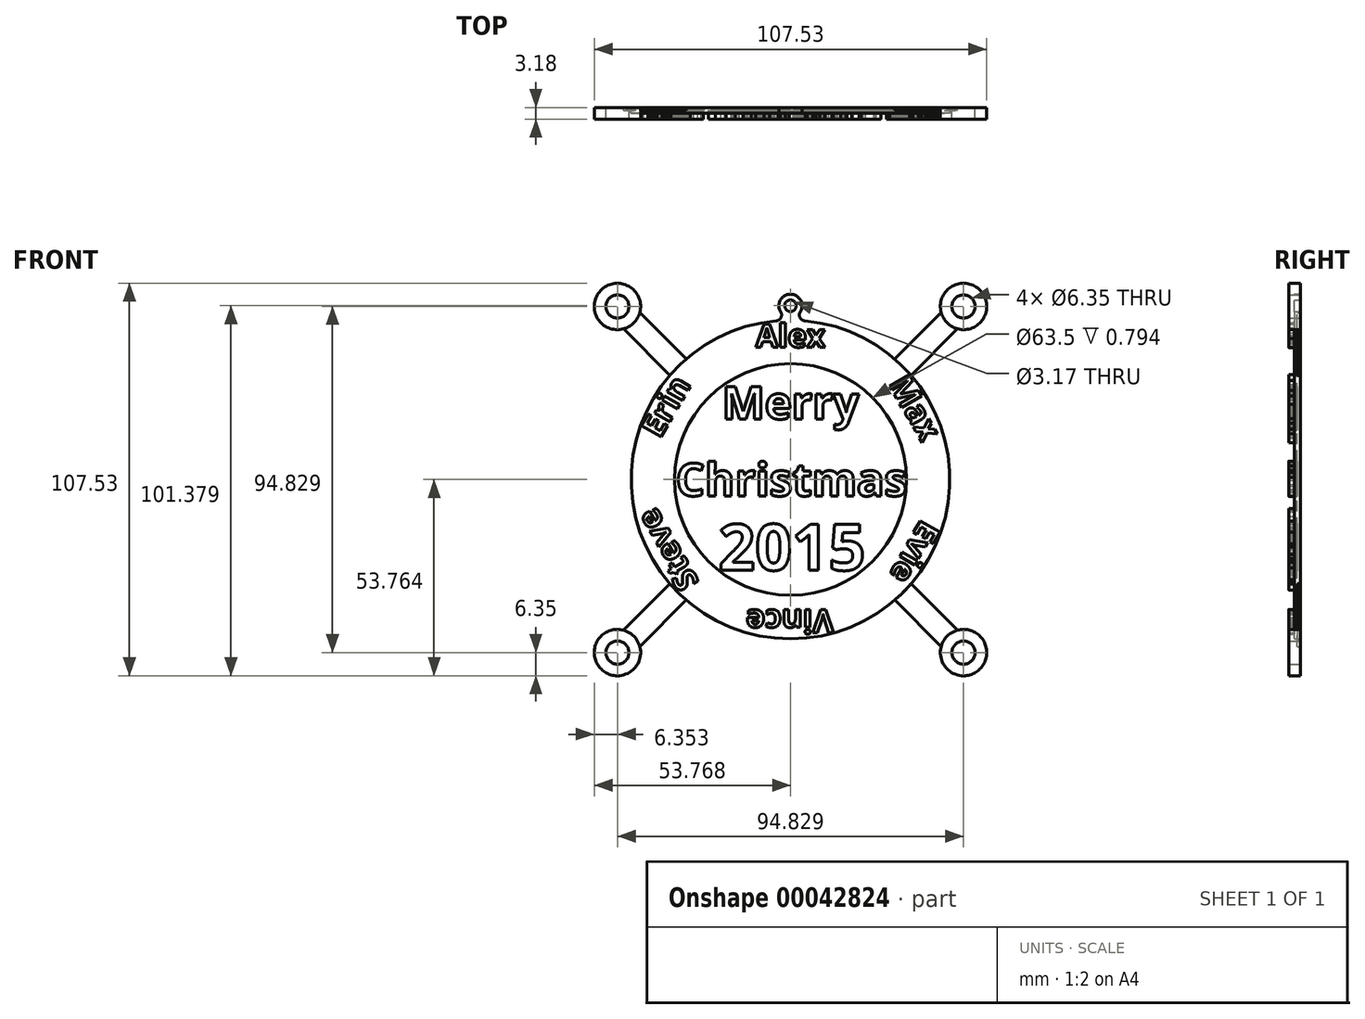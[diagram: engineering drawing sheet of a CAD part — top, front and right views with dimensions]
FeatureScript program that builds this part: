
annotation { "Feature Type Name" : "Feature", "Feature Type Description" : "" }
export const myFeature = defineFeature(function(context is Context, id is Id, definition is map)
    precondition{}
    {
        {
            var Q0;
            Q0=qCreatedBy(makeId("Front.planeOp"),FACE);
            var sketch = newSketch(context, id + "F0", { "sketchPlane" : qUnion([Q0])});
            skText(sketch, "E0", { "text": "2015", "fontName": "OpenSans-Bold.ttf"});
            skPoint(sketch, "E1.center", {"position": v(-132.38, 12.9) * mm});
            skCircle(sketch, "E1.3.1", {"center": v(-84.97, -34.52) * mm, "radius": 6.35 * mm});
            skText(sketch, "E2", { "text": "Christmas", "fontName": "OpenSans-Bold.ttf"});
            skArc(sketch, "E3", {"start": v(-136.26, 56.38) * mm, "mid": v(-132.38, -30.76) * mm, "end": v(-128.5, 56.38) * mm});
            skCircle(sketch, "E4", {"center": v(-132.38, 12.9) * mm, "radius": 31.75 * mm});
            skLineSegment(sketch, "E5", {"start": v(-132.38, 12.9) * mm, "end": v(-132.38, 89.83) * mm, "construction": true});
            skLineSegment(sketch, "E1.2.3", {"start": v(-160.93, -20.14) * mm, "end": v(-173.66, -32.88) * mm});
            skLineSegment(sketch, "E1.2.0", {"start": v(-178.15, -28.39) * mm, "end": v(-165.42, -15.65) * mm});
            skLineSegment(sketch, "E6", {"start": v(-86.61, 54.18) * mm, "end": v(-99.35, 41.44) * mm});
            skPoint(sketch, "E7.orphan", {"position": v(-132.38, 42.36) * mm});
            skCircle(sketch, "E1.1.1", {"center": v(-179.8, 60.3) * mm, "radius": 6.35 * mm});
            skLineSegment(sketch, "E8", {"start": v(-103.84, 45.93) * mm, "end": v(-91.1, 58.67) * mm});
            skLineSegment(sketch, "E1.3.3", {"start": v(-99.35, -15.65) * mm, "end": v(-86.61, -28.39) * mm});
            skLineSegment(sketch, "E9", {"start": v(-132.38, 12.9) * mm, "end": v(-73.52, 71.76) * mm, "construction": true});
            skLineSegment(sketch, "E1.3.0", {"start": v(-91.1, -32.88) * mm, "end": v(-103.84, -20.14) * mm});
            skCircle(sketch, "E10", {"center": v(-84.97, 60.3) * mm, "radius": 6.35 * mm});
            skLineSegment(sketch, "E1.1.0", {"start": v(-173.66, 58.67) * mm, "end": v(-160.93, 45.93) * mm});
            skLineSegment(sketch, "E1.1.3", {"start": v(-165.42, 41.44) * mm, "end": v(-178.15, 54.18) * mm});
            skCircle(sketch, "E1.2.1", {"center": v(-179.8, -34.52) * mm, "radius": 6.35 * mm});
            skText(sketch, "E11", { "text": "Evie", "fontName": "OpenSans-Bold.ttf"});
            skText(sketch, "E12", { "text": "Merry", "fontName": "OpenSans-Bold.ttf"});
            skLineSegment(sketch, "E13.4.0", {"start": v(-104.89, -2.98) * mm, "end": v(-101.38, -5) * mm, "construction": true});
            skText(sketch, "E14", { "text": "Vince", "fontName": "OpenSans-Bold.ttf"});
            skText(sketch, "E15", { "text": "Erin", "fontName": "OpenSans-Bold.ttf"});
            skText(sketch, "E16", { "text": "Max", "fontName": "OpenSans-Bold.ttf"});
            skLineSegment(sketch, "E13.5.0", {"start": v(-104.89, 28.77) * mm, "end": v(-101.38, 30.8) * mm, "construction": true});
            skCircle(sketch, "E1.3.2", {"center": v(-84.97, -34.52) * mm, "radius": 3.18 * mm});
            skCircle(sketch, "E1.2.2", {"center": v(-179.8, -34.52) * mm, "radius": 3.18 * mm});
            skText(sketch, "E17", { "text": "Steve", "fontName": "OpenSans-Bold.ttf"});
            skLineSegment(sketch, "E13.3.0", {"start": v(-132.38, -18.86) * mm, "end": v(-132.38, -22.9) * mm, "construction": true});
            skCircle(sketch, "E1.1.2", {"center": v(-179.8, 60.3) * mm, "radius": 3.18 * mm});
            skLineSegment(sketch, "E13.2.0", {"start": v(-159.88, -2.98) * mm, "end": v(-163.39, -5) * mm, "construction": true});
            skText(sketch, "E18", { "text": "Alex", "fontName": "OpenSans-Bold.ttf"});
            skLineSegment(sketch, "E13.1.0", {"start": v(-159.88, 28.77) * mm, "end": v(-163.39, 30.8) * mm, "construction": true});
            skCircle(sketch, "E19", {"center": v(-84.97, 60.3) * mm, "radius": 3.18 * mm});
            skLineSegment(sketch, "E20.1.0", {"start": v(-160.12, 28.9) * mm, "end": v(-165.6, 32.08) * mm, "construction": true});
            skLineSegment(sketch, "E21.MirrorCS", {"start": v(-101.44, -6.5) * mm, "end": v(-95.1, -6.5) * mm, "construction": true});
            skArc(sketch, "E22", {"start": v(-129.7, 58.8) * mm, "mid": v(-132.38, 63.68) * mm, "end": v(-135.06, 58.8) * mm});
            skLineSegment(sketch, "E23", {"start": v(-132.38, 44.64) * mm, "end": v(-132.38, 48.7) * mm, "construction": true});
            skCircle(sketch, "E24", {"center": v(-132.38, 60.5) * mm, "radius": 1.59 * mm});
            skArc(sketch, "E25.filletArc", {"start": v(-136.26, 56.38) * mm, "mid": v(-134.98, 57.26) * mm, "end": v(-135.06, 58.8) * mm});
            skArc(sketch, "E26.filletArc", {"start": v(-129.7, 58.8) * mm, "mid": v(-129.78, 57.26) * mm, "end": v(-128.5, 56.38) * mm});
            const initialGuessF0  = {"E0": [-0.15212, -0.01197, 1, 0, 0.0127], "E2": [-0.16381, 0.0084, 1, 0, 0.009], "E11": [-0.09647, 0.00225, -0.5, -0.86603, 0.00635], "E12": [-0.1512, 0.02947, 1, 0, 0.009], "E14": [-0.12059, -0.0228, -1, 0, 0.00635], "E15": [-0.16818, 0.02388, 0.5, 0.86603, 0.00635], "E16": [-0.10562, 0.03914, 0.5, -0.86603, 0.00635], "E17": [-0.15733, -0.01522, -0.5, 0.86603, 0.00635], "E18": [-0.1419, 0.04915, 1, 0, 0.00635]};
            skSetInitialGuess(sketch, initialGuessF0);
            skSolve(sketch);
        }
        {
            var Q0;
            Q0=makeQuery(id+"F0.imprint","IMPRINT",FACE,{"disambiguationData":[TD([[makeQuery(id+"F0.imprint","IMPRINT",EDGE,{"derivedFrom":sQuery(id+"F0.wireOp",EDGE,"E18.sketch_text.stroke-0")}),-1.0]])]});
            var Q1;
            Q1=makeQuery(id+"F0.imprint","IMPRINT",FACE,{"disambiguationData":[TD([[makeQuery(id+"F0.imprint","IMPRINT",EDGE,{"derivedFrom":sQuery(id+"F0.wireOp",EDGE,"E18.sketch_text.stroke-12")}),-1.0]])]});
            var Q2;
            Q2=makeQuery(id+"F0.imprint","IMPRINT",FACE,{"disambiguationData":[TD([[makeQuery(id+"F0.imprint","IMPRINT",EDGE,{"derivedFrom":sQuery(id+"F0.wireOp",EDGE,"E18.sketch_text.stroke-16")}),-1.0]])]});
            var Q3;
            Q3=makeQuery(id+"F0.imprint","IMPRINT",FACE,{"disambiguationData":[TD([[makeQuery(id+"F0.imprint","IMPRINT",EDGE,{"derivedFrom":sQuery(id+"F0.wireOp",EDGE,"E18.sketch_text.stroke-36")}),-1.0]])]});
            var Q4;
            Q4=makeQuery(id+"F0.imprint","IMPRINT",FACE,{"disambiguationData":[TD([[makeQuery(id+"F0.imprint","IMPRINT",EDGE,{"derivedFrom":sQuery(id+"F0.wireOp",EDGE,"E16.sketch_text.stroke-0")}),-1.0]])]});
            var Q5;
            Q5=makeQuery(id+"F0.imprint","IMPRINT",FACE,{"disambiguationData":[TD([[makeQuery(id+"F0.imprint","IMPRINT",EDGE,{"derivedFrom":sQuery(id+"F0.wireOp",EDGE,"E16.sketch_text.stroke-19")}),-1.0]])]});
            var Q6;
            Q6=makeQuery(id+"F0.imprint","IMPRINT",FACE,{"disambiguationData":[TD([[makeQuery(id+"F0.imprint","IMPRINT",EDGE,{"derivedFrom":sQuery(id+"F0.wireOp",EDGE,"E16.sketch_text.stroke-44")}),-1.0]])]});
            var Q7;
            Q7=makeQuery(id+"F0.imprint","IMPRINT",FACE,{"disambiguationData":[TD([[makeQuery(id+"F0.imprint","IMPRINT",EDGE,{"derivedFrom":sQuery(id+"F0.wireOp",EDGE,"E12.sketch_text.stroke-0")}),-1.0]])]});
            var Q8;
            Q8=makeQuery(id+"F0.imprint","IMPRINT",FACE,{"disambiguationData":[TD([[makeQuery(id+"F0.imprint","IMPRINT",EDGE,{"derivedFrom":sQuery(id+"F0.wireOp",EDGE,"E12.sketch_text.stroke-19")}),-1.0]])]});
            var Q9;
            Q9=makeQuery(id+"F0.imprint","IMPRINT",FACE,{"disambiguationData":[TD([[makeQuery(id+"F0.imprint","IMPRINT",EDGE,{"derivedFrom":sQuery(id+"F0.wireOp",EDGE,"E12.sketch_text.stroke-39")}),-1.0]])]});
            var Q10;
            Q10=makeQuery(id+"F0.imprint","IMPRINT",FACE,{"disambiguationData":[TD([[makeQuery(id+"F0.imprint","IMPRINT",EDGE,{"derivedFrom":sQuery(id+"F0.wireOp",EDGE,"E12.sketch_text.stroke-52")}),-1.0]])]});
            var Q11;
            Q11=makeQuery(id+"F0.imprint","IMPRINT",FACE,{"disambiguationData":[TD([[makeQuery(id+"F0.imprint","IMPRINT",EDGE,{"derivedFrom":sQuery(id+"F0.wireOp",EDGE,"E12.sketch_text.stroke-65")}),-1.0]])]});
            var Q12;
            Q12=makeQuery(id+"F0.imprint","IMPRINT",FACE,{"disambiguationData":[TD([[makeQuery(id+"F0.imprint","IMPRINT",EDGE,{"derivedFrom":sQuery(id+"F0.wireOp",EDGE,"E2.sketch_text.stroke-0")}),-1.0]])]});
            var Q13;
            Q13=makeQuery(id+"F0.imprint","IMPRINT",FACE,{"disambiguationData":[TD([[makeQuery(id+"F0.imprint","IMPRINT",EDGE,{"derivedFrom":sQuery(id+"F0.wireOp",EDGE,"E2.sketch_text.stroke-15")}),-1.0]])]});
            var Q14;
            Q14=makeQuery(id+"F0.imprint","IMPRINT",FACE,{"disambiguationData":[TD([[makeQuery(id+"F0.imprint","IMPRINT",EDGE,{"derivedFrom":sQuery(id+"F0.wireOp",EDGE,"E2.sketch_text.stroke-32")}),-1.0]])]});
            var Q15;
            Q15=makeQuery(id+"F0.imprint","IMPRINT",FACE,{"disambiguationData":[TD([[makeQuery(id+"F0.imprint","IMPRINT",EDGE,{"derivedFrom":sQuery(id+"F0.wireOp",EDGE,"E2.sketch_text.stroke-50")}),-1.0]])]});
            var Q16;
            Q16=makeQuery(id+"F0.imprint","IMPRINT",FACE,{"disambiguationData":[TD([[makeQuery(id+"F0.imprint","IMPRINT",EDGE,{"derivedFrom":sQuery(id+"F0.wireOp",EDGE,"E2.sketch_text.stroke-54")}),-1.0]])]});
            var Q17;
            Q17=makeQuery(id+"F0.imprint","IMPRINT",FACE,{"disambiguationData":[TD([[makeQuery(id+"F0.imprint","IMPRINT",EDGE,{"derivedFrom":sQuery(id+"F0.wireOp",EDGE,"E2.sketch_text.stroke-45")}),-1.0]])]});
            var Q18;
            Q18=makeQuery(id+"F0.imprint","IMPRINT",FACE,{"disambiguationData":[TD([[makeQuery(id+"F0.imprint","IMPRINT",EDGE,{"derivedFrom":sQuery(id+"F0.wireOp",EDGE,"E2.sketch_text.stroke-80")}),-1.0]])]});
            var Q19;
            Q19=makeQuery(id+"F0.imprint","IMPRINT",FACE,{"disambiguationData":[TD([[makeQuery(id+"F0.imprint","IMPRINT",EDGE,{"derivedFrom":sQuery(id+"F0.wireOp",EDGE,"E2.sketch_text.stroke-98")}),-1.0]])]});
            var Q20;
            Q20=makeQuery(id+"F0.imprint","IMPRINT",FACE,{"disambiguationData":[TD([[makeQuery(id+"F0.imprint","IMPRINT",EDGE,{"derivedFrom":sQuery(id+"F0.wireOp",EDGE,"E2.sketch_text.stroke-126")}),-1.0]])]});
            var Q21;
            Q21=makeQuery(id+"F0.imprint","IMPRINT",FACE,{"disambiguationData":[TD([[makeQuery(id+"F0.imprint","IMPRINT",EDGE,{"derivedFrom":sQuery(id+"F0.wireOp",EDGE,"E2.sketch_text.stroke-151")}),-1.0]])]});
            var Q22;
            Q22=makeQuery(id+"F0.imprint","IMPRINT",FACE,{"disambiguationData":[TD([[makeQuery(id+"F0.imprint","IMPRINT",EDGE,{"derivedFrom":sQuery(id+"F0.wireOp",EDGE,"E0.sketch_text.stroke-0")}),-1.0]])]});
            var Q23;
            Q23=makeQuery(id+"F0.imprint","IMPRINT",FACE,{"disambiguationData":[TD([[makeQuery(id+"F0.imprint","IMPRINT",EDGE,{"derivedFrom":sQuery(id+"F0.wireOp",EDGE,"E0.sketch_text.stroke-24")}),-1.0]])]});
            var Q24;
            Q24=makeQuery(id+"F0.imprint","IMPRINT",FACE,{"disambiguationData":[TD([[makeQuery(id+"F0.imprint","IMPRINT",EDGE,{"derivedFrom":sQuery(id+"F0.wireOp",EDGE,"E0.sketch_text.stroke-40")}),-1.0]])]});
            var Q25;
            Q25=makeQuery(id+"F0.imprint","IMPRINT",FACE,{"disambiguationData":[TD([[makeQuery(id+"F0.imprint","IMPRINT",EDGE,{"derivedFrom":sQuery(id+"F0.wireOp",EDGE,"E0.sketch_text.stroke-50")}),-1.0]])]});
            var Q26;
            Q26=makeQuery(id+"F0.imprint","IMPRINT",FACE,{"disambiguationData":[TD([[makeQuery(id+"F0.imprint","IMPRINT",EDGE,{"derivedFrom":sQuery(id+"F0.wireOp",EDGE,"E11.sketch_text.stroke-0")}),-1.0]])]});
            var Q27;
            Q27=makeQuery(id+"F0.imprint","IMPRINT",FACE,{"disambiguationData":[TD([[makeQuery(id+"F0.imprint","IMPRINT",EDGE,{"derivedFrom":sQuery(id+"F0.wireOp",EDGE,"E11.sketch_text.stroke-12")}),-1.0]])]});
            var Q28;
            Q28=makeQuery(id+"F0.imprint","IMPRINT",FACE,{"disambiguationData":[TD([[makeQuery(id+"F0.imprint","IMPRINT",EDGE,{"derivedFrom":sQuery(id+"F0.wireOp",EDGE,"E11.sketch_text.stroke-27")}),-1.0]])]});
            var Q29;
            Q29=makeQuery(id+"F0.imprint","IMPRINT",FACE,{"disambiguationData":[TD([[makeQuery(id+"F0.imprint","IMPRINT",EDGE,{"derivedFrom":sQuery(id+"F0.wireOp",EDGE,"E11.sketch_text.stroke-22")}),-1.0]])]});
            var Q30;
            Q30=makeQuery(id+"F0.imprint","IMPRINT",FACE,{"disambiguationData":[TD([[makeQuery(id+"F0.imprint","IMPRINT",EDGE,{"derivedFrom":sQuery(id+"F0.wireOp",EDGE,"E11.sketch_text.stroke-31")}),-1.0]])]});
            var Q31;
            Q31=makeQuery(id+"F0.imprint","IMPRINT",FACE,{"disambiguationData":[TD([[makeQuery(id+"F0.imprint","IMPRINT",EDGE,{"derivedFrom":sQuery(id+"F0.wireOp",EDGE,"E14.sketch_text.stroke-0")}),-1.0]])]});
            var Q32;
            Q32=makeQuery(id+"F0.imprint","IMPRINT",FACE,{"disambiguationData":[TD([[makeQuery(id+"F0.imprint","IMPRINT",EDGE,{"derivedFrom":sQuery(id+"F0.wireOp",EDGE,"E14.sketch_text.stroke-15")}),-1.0]])]});
            var Q33;
            Q33=makeQuery(id+"F0.imprint","IMPRINT",FACE,{"disambiguationData":[TD([[makeQuery(id+"F0.imprint","IMPRINT",EDGE,{"derivedFrom":sQuery(id+"F0.wireOp",EDGE,"E14.sketch_text.stroke-10")}),-1.0]])]});
            var Q34;
            Q34=makeQuery(id+"F0.imprint","IMPRINT",FACE,{"disambiguationData":[TD([[makeQuery(id+"F0.imprint","IMPRINT",EDGE,{"derivedFrom":sQuery(id+"F0.wireOp",EDGE,"E14.sketch_text.stroke-19")}),-1.0]])]});
            var Q35;
            Q35=makeQuery(id+"F0.imprint","IMPRINT",FACE,{"disambiguationData":[TD([[makeQuery(id+"F0.imprint","IMPRINT",EDGE,{"derivedFrom":sQuery(id+"F0.wireOp",EDGE,"E14.sketch_text.stroke-36")}),-1.0]])]});
            var Q36;
            Q36=makeQuery(id+"F0.imprint","IMPRINT",FACE,{"disambiguationData":[TD([[makeQuery(id+"F0.imprint","IMPRINT",EDGE,{"derivedFrom":sQuery(id+"F0.wireOp",EDGE,"E14.sketch_text.stroke-50")}),-1.0]])]});
            var Q37;
            Q37=makeQuery(id+"F0.imprint","IMPRINT",FACE,{"disambiguationData":[TD([[makeQuery(id+"F0.imprint","IMPRINT",EDGE,{"derivedFrom":sQuery(id+"F0.wireOp",EDGE,"E17.sketch_text.stroke-0")}),-1.0]])]});
            var Q38;
            Q38=makeQuery(id+"F0.imprint","IMPRINT",FACE,{"disambiguationData":[TD([[makeQuery(id+"F0.imprint","IMPRINT",EDGE,{"derivedFrom":sQuery(id+"F0.wireOp",EDGE,"E17.sketch_text.stroke-28")}),-1.0]])]});
            var Q39;
            Q39=makeQuery(id+"F0.imprint","IMPRINT",FACE,{"disambiguationData":[TD([[makeQuery(id+"F0.imprint","IMPRINT",EDGE,{"derivedFrom":sQuery(id+"F0.wireOp",EDGE,"E17.sketch_text.stroke-46")}),-1.0]])]});
            var Q40;
            Q40=makeQuery(id+"F0.imprint","IMPRINT",FACE,{"disambiguationData":[TD([[makeQuery(id+"F0.imprint","IMPRINT",EDGE,{"derivedFrom":sQuery(id+"F0.wireOp",EDGE,"E17.sketch_text.stroke-66")}),-1.0]])]});
            var Q41;
            Q41=makeQuery(id+"F0.imprint","IMPRINT",FACE,{"disambiguationData":[TD([[makeQuery(id+"F0.imprint","IMPRINT",EDGE,{"derivedFrom":sQuery(id+"F0.wireOp",EDGE,"E17.sketch_text.stroke-76")}),-1.0]])]});
            var Q42;
            Q42=makeQuery(id+"F0.imprint","IMPRINT",FACE,{"disambiguationData":[TD([[makeQuery(id+"F0.imprint","IMPRINT",EDGE,{"derivedFrom":sQuery(id+"F0.wireOp",EDGE,"E15.sketch_text.stroke-0")}),-1.0]])]});
            var Q43;
            Q43=makeQuery(id+"F0.imprint","IMPRINT",FACE,{"disambiguationData":[TD([[makeQuery(id+"F0.imprint","IMPRINT",EDGE,{"derivedFrom":sQuery(id+"F0.wireOp",EDGE,"E15.sketch_text.stroke-12")}),-1.0]])]});
            var Q44;
            Q44=makeQuery(id+"F0.imprint","IMPRINT",FACE,{"disambiguationData":[TD([[makeQuery(id+"F0.imprint","IMPRINT",EDGE,{"derivedFrom":sQuery(id+"F0.wireOp",EDGE,"E15.sketch_text.stroke-30")}),-1.0]])]});
            var Q45;
            Q45=makeQuery(id+"F0.imprint","IMPRINT",FACE,{"disambiguationData":[TD([[makeQuery(id+"F0.imprint","IMPRINT",EDGE,{"derivedFrom":sQuery(id+"F0.wireOp",EDGE,"E15.sketch_text.stroke-25")}),-1.0]])]});
            var Q46;
            Q46=makeQuery(id+"F0.imprint","IMPRINT",FACE,{"disambiguationData":[TD([[makeQuery(id+"F0.imprint","IMPRINT",EDGE,{"derivedFrom":sQuery(id+"F0.wireOp",EDGE,"E15.sketch_text.stroke-34")}),-1.0]])]});
            var Q47;
            Q47=makeQuery(id+"F0.imprint","IMPRINT",FACE,{"disambiguationData":[TD([[makeQuery(id+"F0.imprint","IMPRINT",EDGE,{"derivedFrom":sQuery(id+"F0.wireOp",EDGE,"E1.1.2")}),-1.0]])]});
            var Q48;
            Q48=makeQuery(id+"F0.imprint","IMPRINT",FACE,{"disambiguationData":[TD([[makeQuery(id+"F0.imprint","IMPRINT",EDGE,{"derivedFrom":sQuery(id+"F0.wireOp",EDGE,"E19")}),-1.0]])]});
            var Q49;
            Q49=makeQuery(id+"F0.imprint","IMPRINT",FACE,{"disambiguationData":[TD([[makeQuery(id+"F0.imprint","IMPRINT",EDGE,{"derivedFrom":sQuery(id+"F0.wireOp",EDGE,"E1.3.2")}),-1.0]])]});
            var Q50;
            Q50=makeQuery(id+"F0.imprint","IMPRINT",FACE,{"disambiguationData":[TD([[makeQuery(id+"F0.imprint","IMPRINT",EDGE,{"derivedFrom":sQuery(id+"F0.wireOp",EDGE,"E1.2.2")}),-1.0]])]});
            extrude(context, id + "F1", {"entities" : qUnion([Q0, Q1, Q2, Q3, Q4, Q5, Q6, Q7, Q8, Q9, Q10, Q11, Q12, Q13, Q14, Q15, Q16, Q17, Q18, Q19, Q20, Q21, Q22, Q23, Q24, Q25, Q26, Q27, Q28, Q29, Q30, Q31, Q32, Q33, Q34, Q35, Q36, Q37, Q38, Q39, Q40, Q41, Q42, Q43, Q44, Q45, Q46, Q47, Q48, Q49, Q50]), "depth" : 3.17 * mm});
        }
        {
            var Q0;
            Q0=makeQuery(id+"F0.imprint","IMPRINT",FACE,{"disambiguationData":[TD([[makeQuery(id+"F0.imprint","IMPRINT",EDGE,{"derivedFrom":sQuery(id+"F0.wireOp",EDGE,"E4")}),-1.0]])]});
            var Q1;
            Q1=makeQuery(id+"F0.imprint","IMPRINT",FACE,{"disambiguationData":[TD([[makeQuery(id+"F0.imprint","IMPRINT",EDGE,{"derivedFrom":sQuery(id+"F0.wireOp",EDGE,"E17.sketch_text.stroke-46")}),1.0]])]});
            var Q2;
            Q2=makeQuery(id+"F0.imprint","IMPRINT",FACE,{"disambiguationData":[TD([[makeQuery(id+"F0.imprint","IMPRINT",EDGE,{"derivedFrom":sQuery(id+"F0.wireOp",EDGE,"E17.sketch_text.stroke-76")}),1.0]])]});
            var Q3;
            Q3=makeQuery(id+"F0.imprint","IMPRINT",FACE,{"disambiguationData":[TD([[makeQuery(id+"F0.imprint","IMPRINT",EDGE,{"derivedFrom":sQuery(id+"F0.wireOp",EDGE,"E14.sketch_text.stroke-50")}),1.0]])]});
            var Q4;
            Q4=makeQuery(id+"F0.imprint","IMPRINT",FACE,{"disambiguationData":[TD([[makeQuery(id+"F0.imprint","IMPRINT",EDGE,{"derivedFrom":sQuery(id+"F0.wireOp",EDGE,"E11.sketch_text.stroke-31")}),1.0]])]});
            var Q5;
            Q5=makeQuery(id+"F0.imprint","IMPRINT",FACE,{"disambiguationData":[TD([[makeQuery(id+"F0.imprint","IMPRINT",EDGE,{"derivedFrom":sQuery(id+"F0.wireOp",EDGE,"E16.sketch_text.stroke-37")}),1.0]])]});
            var Q6;
            Q6=makeQuery(id+"F0.imprint","IMPRINT",FACE,{"disambiguationData":[TD([[makeQuery(id+"F0.imprint","IMPRINT",EDGE,{"derivedFrom":sQuery(id+"F0.wireOp",EDGE,"E18.sketch_text.stroke-16")}),1.0]])]});
            var Q7;
            Q7=makeQuery(id+"F0.imprint","IMPRINT",FACE,{"disambiguationData":[TD([[makeQuery(id+"F0.imprint","IMPRINT",EDGE,{"derivedFrom":sQuery(id+"F0.wireOp",EDGE,"E18.sketch_text.stroke-8")}),1.0]])]});
            extrude(context, id + "F2", {"entities" : qUnion([Q0, Q1, Q2, Q3, Q4, Q5, Q6, Q7]), "operationType" : NewBodyOperationType.ADD, "depth" : 1.59 * mm});
        }
        {
            var Q0;
            Q0=makeQuery(id+"F0.imprint","IMPRINT",FACE,{"disambiguationData":[TD([[makeQuery(id+"F0.imprint","IMPRINT",EDGE,{"derivedFrom":sQuery(id+"F0.wireOp",EDGE,"E0.sketch_text.stroke-0")}),1.0]])]});
            var Q1;
            Q1=makeQuery(id+"F0.imprint","IMPRINT",FACE,{"disambiguationData":[TD([[makeQuery(id+"F0.imprint","IMPRINT",EDGE,{"derivedFrom":sQuery(id+"F0.wireOp",EDGE,"E0.sketch_text.stroke-32")}),1.0]])]});
            var Q2;
            {var subQ0=sQuery(id+"F0.wireOp",EDGE,"E6");Q2=makeQuery(id+"F0.imprint","IMPRINT",FACE,{"disambiguationData":[TD([[makeQuery(id+"F0.imprint","IMPRINT",EDGE,{"derivedFrom":subQ0}),-1.0]])]});}
            var Q3;
            {var subQ0=sQuery(id+"F0.wireOp",EDGE,"E1.3.3");Q3=makeQuery(id+"F0.imprint","IMPRINT",FACE,{"disambiguationData":[TD([[makeQuery(id+"F0.imprint","IMPRINT",EDGE,{"derivedFrom":subQ0}),-1.0]])]});}
            var Q4;
            {var subQ0=sQuery(id+"F0.wireOp",EDGE,"E1.2.3");Q4=makeQuery(id+"F0.imprint","IMPRINT",FACE,{"disambiguationData":[TD([[makeQuery(id+"F0.imprint","IMPRINT",EDGE,{"derivedFrom":subQ0}),-1.0]])]});}
            var Q5;
            {var subQ0=sQuery(id+"F0.wireOp",EDGE,"E1.1.0");Q5=makeQuery(id+"F0.imprint","IMPRINT",FACE,{"disambiguationData":[TD([[makeQuery(id+"F0.imprint","IMPRINT",EDGE,{"derivedFrom":subQ0}),-1.0]])]});}
            var Q6;
            Q6=makeQuery(id+"F0.imprint","IMPRINT",FACE,{"disambiguationData":[TD([[makeQuery(id+"F0.imprint","IMPRINT",EDGE,{"derivedFrom":sQuery(id+"F0.wireOp",EDGE,"E12.sketch_text.stroke-19")}),1.0]])]});
            var Q7;
            Q7=makeQuery(id+"F0.imprint","IMPRINT",FACE,{"disambiguationData":[TD([[makeQuery(id+"F0.imprint","IMPRINT",EDGE,{"derivedFrom":sQuery(id+"F0.wireOp",EDGE,"E2.sketch_text.stroke-144")}),1.0]])]});
            extrude(context, id + "F3", {"entities" : qUnion([Q0, Q1, Q2, Q3, Q4, Q5, Q6, Q7]), "operationType" : NewBodyOperationType.ADD, "depth" : 0.8 * mm});
        }
    });
